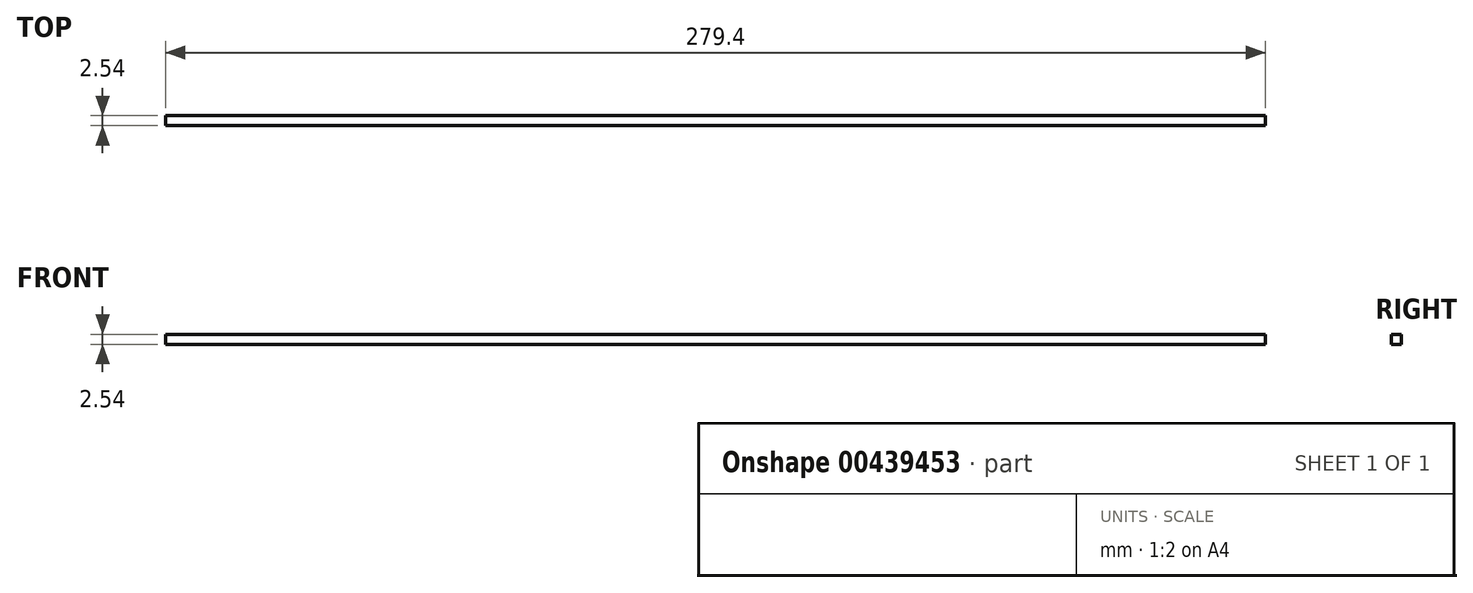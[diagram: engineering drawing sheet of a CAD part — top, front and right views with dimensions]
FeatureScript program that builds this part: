
annotation { "Feature Type Name" : "Feature", "Feature Type Description" : "" }
export const myFeature = defineFeature(function(context is Context, id is Id, definition is map)
    precondition{}
    {
        {
            var Q0;
            Q0=qCreatedBy(makeId("Front.planeOp"),FACE);
            var sketch = newSketch(context, id + "F0", { "sketchPlane" : qUnion([Q0])});
            skLineSegment(sketch, "E0.bottom", {"start": v(-139.27, 0) * mm, "end": v(140.13, 0) * mm});
            skLineSegment(sketch, "E0.top", {"start": v(-139.27, -2.54) * mm, "end": v(140.13, -2.54) * mm});
            skLineSegment(sketch, "E0.left", {"start": v(-139.27, 0) * mm, "end": v(-139.27, -2.54) * mm});
            skLineSegment(sketch, "E0.right", {"start": v(140.13, 0) * mm, "end": v(140.13, -2.54) * mm});
            skSolve(sketch);
        }
        {
            var Q0;
            Q0=makeQuery(id+"F0.imprint","IMPRINT",FACE,{"disambiguationData":[TD([[makeQuery(id+"F0.imprint","IMPRINT",EDGE,{"derivedFrom":sQuery(id+"F0.wireOp",EDGE,"E0.bottom")}),-1.0]])]});
            extrude(context, id + "F1", {"entities" : qUnion([Q0]), "depth" : 2.54 * mm});
        }
    });
